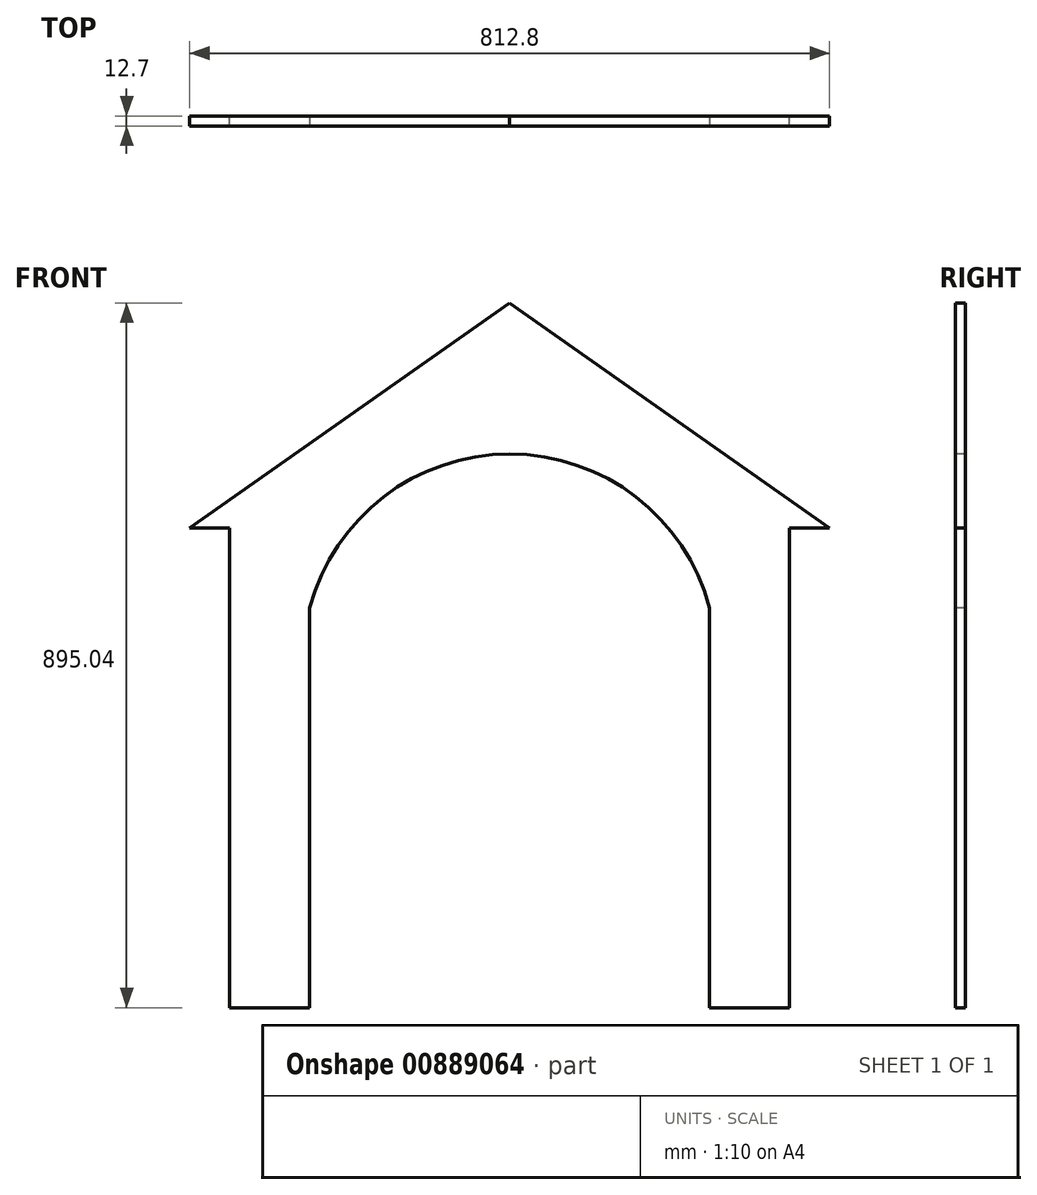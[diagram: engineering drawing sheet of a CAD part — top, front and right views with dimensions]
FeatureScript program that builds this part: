
annotation { "Feature Type Name" : "Feature", "Feature Type Description" : "" }
export const myFeature = defineFeature(function(context is Context, id is Id, definition is map)
    precondition{}
    {
        {
            var Q0;
            Q0=qCreatedBy(makeId("Front.planeOp"),FACE);
            var sketch = newSketch(context, id + "F0", { "sketchPlane" : qUnion([Q0])});
            skLineSegment(sketch, "E0.top", {"start": v(-355.6, -304.8) * mm, "end": v(355.6, -304.8) * mm});
            skLineSegment(sketch, "E0.left", {"start": v(-355.6, 304.8) * mm, "end": v(-355.6, -304.8) * mm});
            skLineSegment(sketch, "E0.right", {"start": v(355.6, 304.8) * mm, "end": v(355.6, -304.8) * mm});
            skPoint(sketch, "E0.middle", {"position": v(0, 0) * mm});
            skLineSegment(sketch, "E1", {"start": v(-406.4, 304.8) * mm, "end": v(-355.6, 304.8) * mm});
            skLineSegment(sketch, "E2", {"start": v(355.6, 304.8) * mm, "end": v(406.4, 304.8) * mm});
            skLineSegment(sketch, "E3", {"start": v(-406.4, 304.8) * mm, "end": v(0, 590.24) * mm});
            skLineSegment(sketch, "E4", {"start": v(0, 590.24) * mm, "end": v(406.4, 304.8) * mm});
            skPoint(sketch, "E5", {"position": v(0, 304.8) * mm});
            skSolve(sketch);
        }
        {
            var Q0;
            Q0=qSketchRegion(id+"F0",true);
            extrude(context, id + "F1", {"entities" : qUnion([Q0]), "depth" : 12.7 * mm, "offsetDistance" : 25.4 * mm});
        }
        {
            var Q0;
            Q0=makeQuery(id+"F1.opExtrude","CAP_FACE",FACE,{"disambiguationData":[OSD([sQuery(id+"F0.wireOp",EDGE,"E0.top"),sQuery(id+"F0.wireOp",EDGE,"E0.left"),sQuery(id+"F0.wireOp",EDGE,"E0.right"),sQuery(id+"F0.wireOp",EDGE,"E1"),sQuery(id+"F0.wireOp",EDGE,"E2"),sQuery(id+"F0.wireOp",EDGE,"E3"),sQuery(id+"F0.wireOp",EDGE,"E4")])],"isStart":false});
            var sketch = newSketch(context, id + "F2", { "sketchPlane" : qUnion([Q0])});
            skLineSegment(sketch, "E6.bottom", {"start": v(-254, -304.8) * mm, "end": v(254, -304.8) * mm});
            skLineSegment(sketch, "E6.left", {"start": v(-254, -304.8) * mm, "end": v(-254, 203.2) * mm});
            skLineSegment(sketch, "E6.right", {"start": v(254, -304.8) * mm, "end": v(254, 203.2) * mm});
            skArc(sketch, "E7", {"start": v(254, 203.2) * mm, "mid": v(0, 398.56) * mm, "end": v(-254, 203.2) * mm});
            skSolve(sketch);
        }
        {
            var Q0;
            Q0 = qSketchRegion(id + "F2", true);
            extrude(context, id + "F3", {"entities" : qUnion([Q0]), "operationType" : NewBodyOperationType.REMOVE, "oppositeDirection" : true, "depth" : 25.4 * mm, "offsetDistance" : 25.4 * mm});
        }
    });
